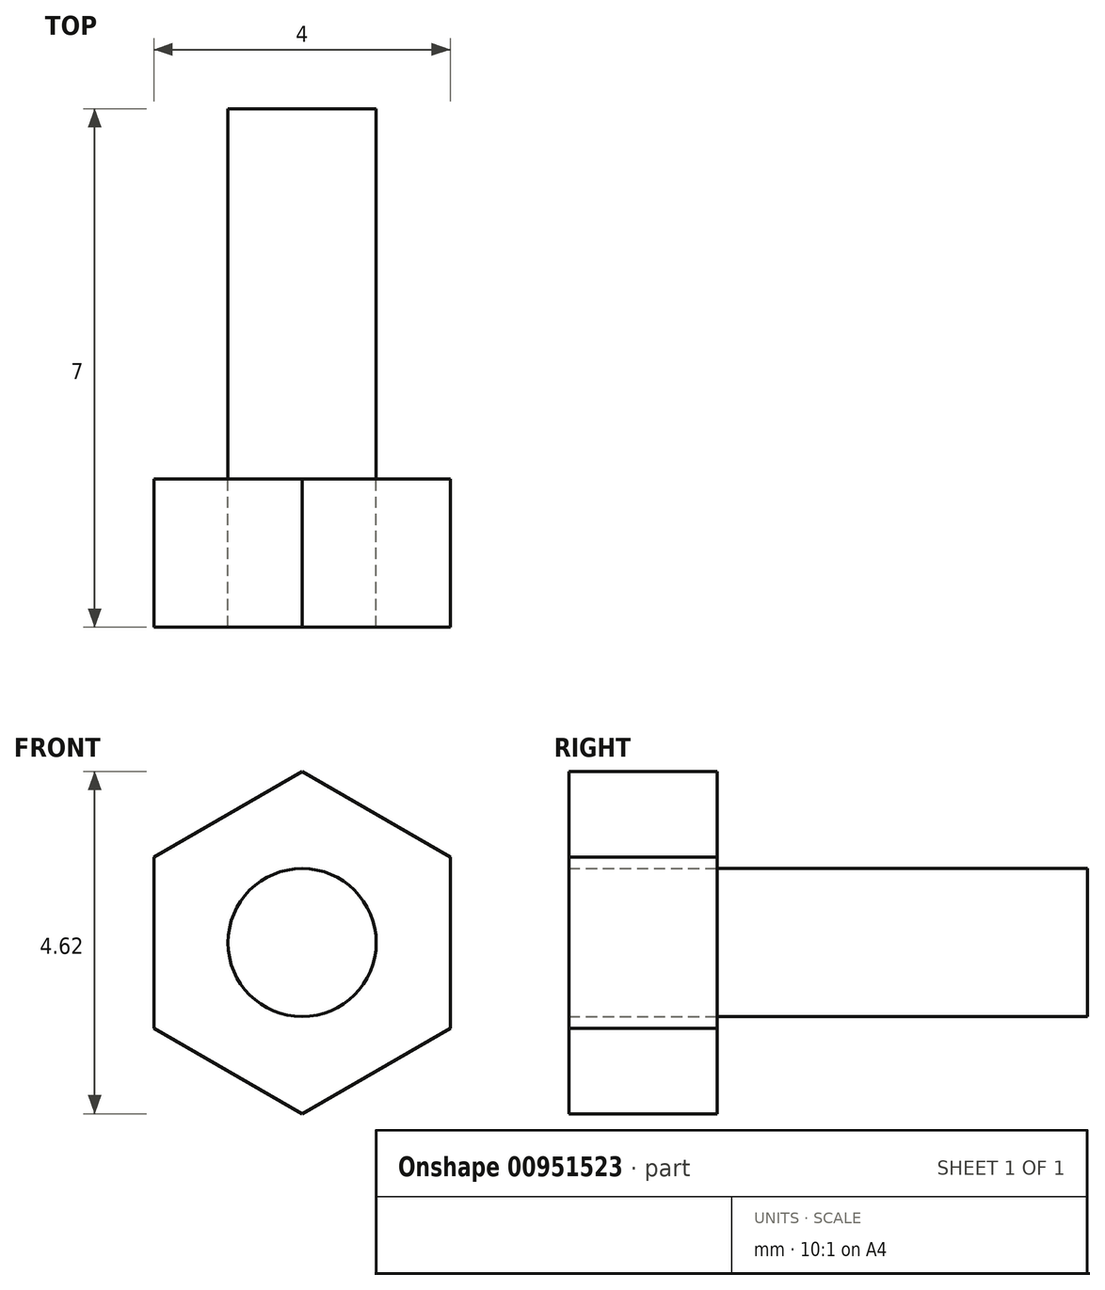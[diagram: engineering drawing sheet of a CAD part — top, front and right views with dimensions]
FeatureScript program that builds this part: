
annotation { "Feature Type Name" : "Feature", "Feature Type Description" : "" }
export const myFeature = defineFeature(function(context is Context, id is Id, definition is map)
    precondition{}
    {
        {
            var Q0;
            Q0=qCreatedBy(makeId("Front.planeOp"),FACE);
            var sketch = newSketch(context, id + "F0", { "sketchPlane" : qUnion([Q0])});
            skCircle(sketch, "E0", {"center": v(0, 0) * mm, "radius": 1 * mm});
            skCircle(sketch, "E1.cCircle", {"center": v(0, 0) * mm, "radius": 2 * mm, "construction": true});
            skLineSegment(sketch, "E1.0", {"start": v(-2, -1.15) * mm, "end": v(-2, 1.15) * mm});
            skLineSegment(sketch, "E1.1", {"start": v(-2, 1.15) * mm, "end": v(0, 2.3) * mm});
            skLineSegment(sketch, "E1.2", {"start": v(0, 2.3) * mm, "end": v(2, 1.15) * mm});
            skLineSegment(sketch, "E1.3", {"start": v(2, 1.15) * mm, "end": v(2, -1.15) * mm});
            skLineSegment(sketch, "E1.4", {"start": v(2, -1.15) * mm, "end": v(0, -2.3) * mm});
            skLineSegment(sketch, "E1.5", {"start": v(0, -2.3) * mm, "end": v(-2, -1.15) * mm});
            skPoint(sketch, "E1.0.midPoint", {"position": v(-2, 0) * mm});
            skSolve(sketch);
        }
        {
            var Q0;
            Q0 = qSketchRegion(id + "F0", true);
            var Q1;
            Q1=makeQuery(id+"F0.imprint","IMPRINT",FACE,{"disambiguationData":[TD([[makeQuery(id+"F0.imprint","IMPRINT",EDGE,{"derivedFrom":sQuery(id+"F0.wireOp",EDGE,"E0")}),1.0]])]});
            extrude(context, id + "F1", {"entities" : qUnion([Q0, Q1]), "depth" : 2 * mm, "offsetDistance" : 25 * mm});
        }
        {
            var Q0;
            Q0=makeQuery(id+"F1.opExtrude","CAP_FACE",FACE,{"disambiguationData":[OSD([sQuery(id+"F0.wireOp",EDGE,"E1.0"),sQuery(id+"F0.wireOp",EDGE,"E1.1"),sQuery(id+"F0.wireOp",EDGE,"E1.2"),sQuery(id+"F0.wireOp",EDGE,"E1.3"),sQuery(id+"F0.wireOp",EDGE,"E1.4"),sQuery(id+"F0.wireOp",EDGE,"E1.5")])],"isStart":true});
            var sketch = newSketch(context, id + "F2", { "sketchPlane" : qUnion([Q0])});
            skCircle(sketch, "E2", {"center": v(0, 0) * mm, "radius": 1 * mm});
            skSolve(sketch);
        }
        {
            var Q0;
            Q0 = qSketchRegion(id + "F2", true);
            extrude(context, id + "F3", {"entities" : qUnion([Q0]), "operationType" : NewBodyOperationType.ADD, "depth" : 5 * mm, "offsetDistance" : 25 * mm});
        }
        {
            var Q0;
            Q0=makeQuery(id+"F0.imprint","IMPRINT",FACE,{"disambiguationData":[TD([[makeQuery(id+"F0.imprint","IMPRINT",EDGE,{"derivedFrom":sQuery(id+"F0.wireOp",EDGE,"E0")}),-1.0]])]});
            extrude(context, id + "F4", {"entities" : qUnion([Q0]), "depth" : 2 * mm, "offsetDistance" : 25 * mm});
        }
    });
